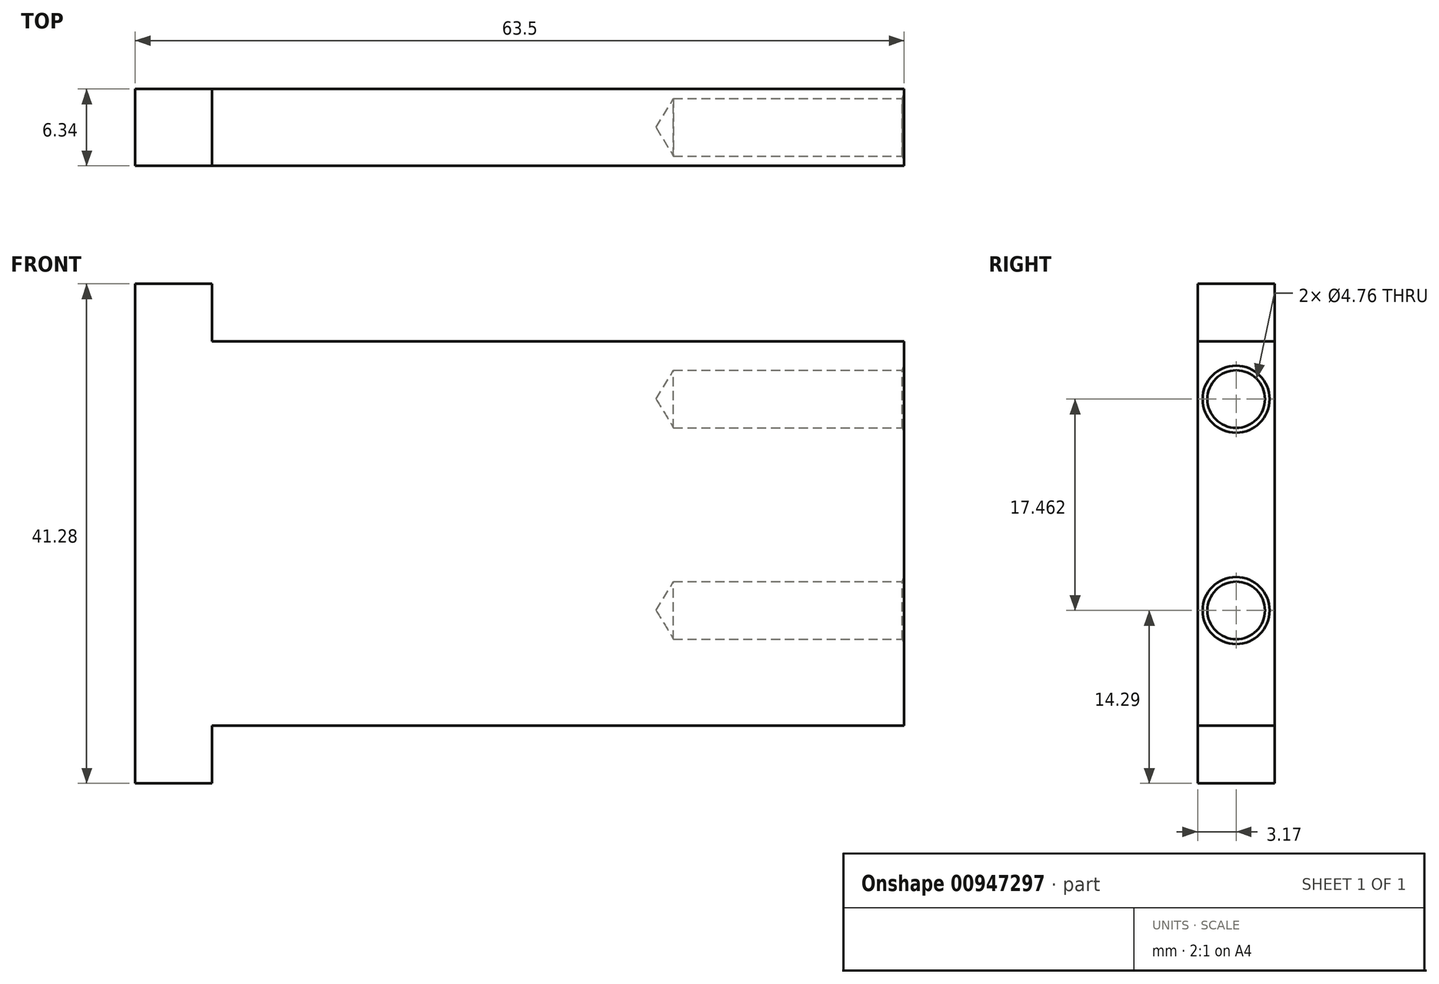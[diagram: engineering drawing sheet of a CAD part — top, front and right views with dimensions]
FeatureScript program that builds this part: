
annotation { "Feature Type Name" : "Feature", "Feature Type Description" : "" }
export const myFeature = defineFeature(function(context is Context, id is Id, definition is map)
    precondition{}
    {
        {
            var Q0;
            Q0=qCreatedBy(makeId("Front.planeOp"),FACE);
            var sketch = newSketch(context, id + "F0", { "sketchPlane" : qUnion([Q0])});
            skLineSegment(sketch, "E0", {"start": v(0, 0) * mm, "end": v(-88.26, 0) * mm, "construction": true});
            skLineSegment(sketch, "E1", {"start": v(-63.5, 20.64) * mm, "end": v(-63.5, -20.64) * mm});
            skLineSegment(sketch, "E2", {"start": v(-63.5, 20.64) * mm, "end": v(-57.15, 20.64) * mm});
            skLineSegment(sketch, "E3", {"start": v(-57.15, 20.64) * mm, "end": v(-57.15, 15.88) * mm});
            skLineSegment(sketch, "E4", {"start": v(-57.15, 15.87) * mm, "end": v(0, 15.88) * mm});
            skLineSegment(sketch, "E5", {"start": v(0, 15.88) * mm, "end": v(0, -15.88) * mm});
            skLineSegment(sketch, "E6", {"start": v(0, -15.88) * mm, "end": v(-57.15, -15.88) * mm});
            skLineSegment(sketch, "E7", {"start": v(-57.15, -15.88) * mm, "end": v(-57.15, -20.64) * mm});
            skLineSegment(sketch, "E8", {"start": v(-57.15, -20.64) * mm, "end": v(-63.5, -20.64) * mm});
            skSolve(sketch);
        }
        {
            var Q0;
            Q0 = qSketchRegion(id + "F0", true);
            extrude(context, id + "F1", {"entities" : qUnion([Q0]), "endBound" : BoundingType.SYMMETRIC, "depth" : 6.35 * mm, "offsetDistance" : 25.4 * mm});
        }
        {
            var Q0;
            Q0=makeQuery(id+"F1.opExtrude","SWEPT_FACE",FACE,{"disambiguationData":[OSD([sQuery(id+"F0.wireOp",EDGE,"E5")])]});
            var sketch = newSketch(context, id + "F2", { "sketchPlane" : qUnion([Q0])});
            skPoint(sketch, "E9", {"position": v(0, 11.11) * mm});
            skPoint(sketch, "E10", {"position": v(0, -6.35) * mm});
            skSolve(sketch);
        }
        {
            var Q0;
            Q0=sQuery(id+"F2.wireOp",VERTEX,"E9");
            var Q1;
            Q1=sQuery(id+"F2.wireOp",VERTEX,"E10");
            var Q2;
            Q2=makeQuery(id+"F1.opExtrude","SWEPT_BODY",BODY,{"disambiguationData":[OSD([sQuery(id+"F0.wireOp",EDGE,"E1"),sQuery(id+"F0.wireOp",EDGE,"E2"),sQuery(id+"F0.wireOp",EDGE,"E3"),sQuery(id+"F0.wireOp",EDGE,"E4"),sQuery(id+"F0.wireOp",EDGE,"E5"),sQuery(id+"F0.wireOp",EDGE,"E6"),sQuery(id+"F0.wireOp",EDGE,"E7"),sQuery(id+"F0.wireOp",EDGE,"E8")])]});
            hole(context, id + "F3", {"style" : HoleStyle.C_SINK, "endStyle" : HoleEndStyle.BLIND, "holeDiameter" : 4.76 * mm, "cSinkDiameter" : 5.54 * mm, "cSinkAngle" : 135 * degree, "majorDiameter" : 6.35 * mm, "holeDepth" : 19.05 * mm, "isTappedThrough" : true, "tappedDepth" : 12.7 * mm, "tapClearance" : 3, "startFromSketch" : true, "locations" : qUnion([Q0, Q1]), "scope" : qUnion([Q2])});
        }
    });
